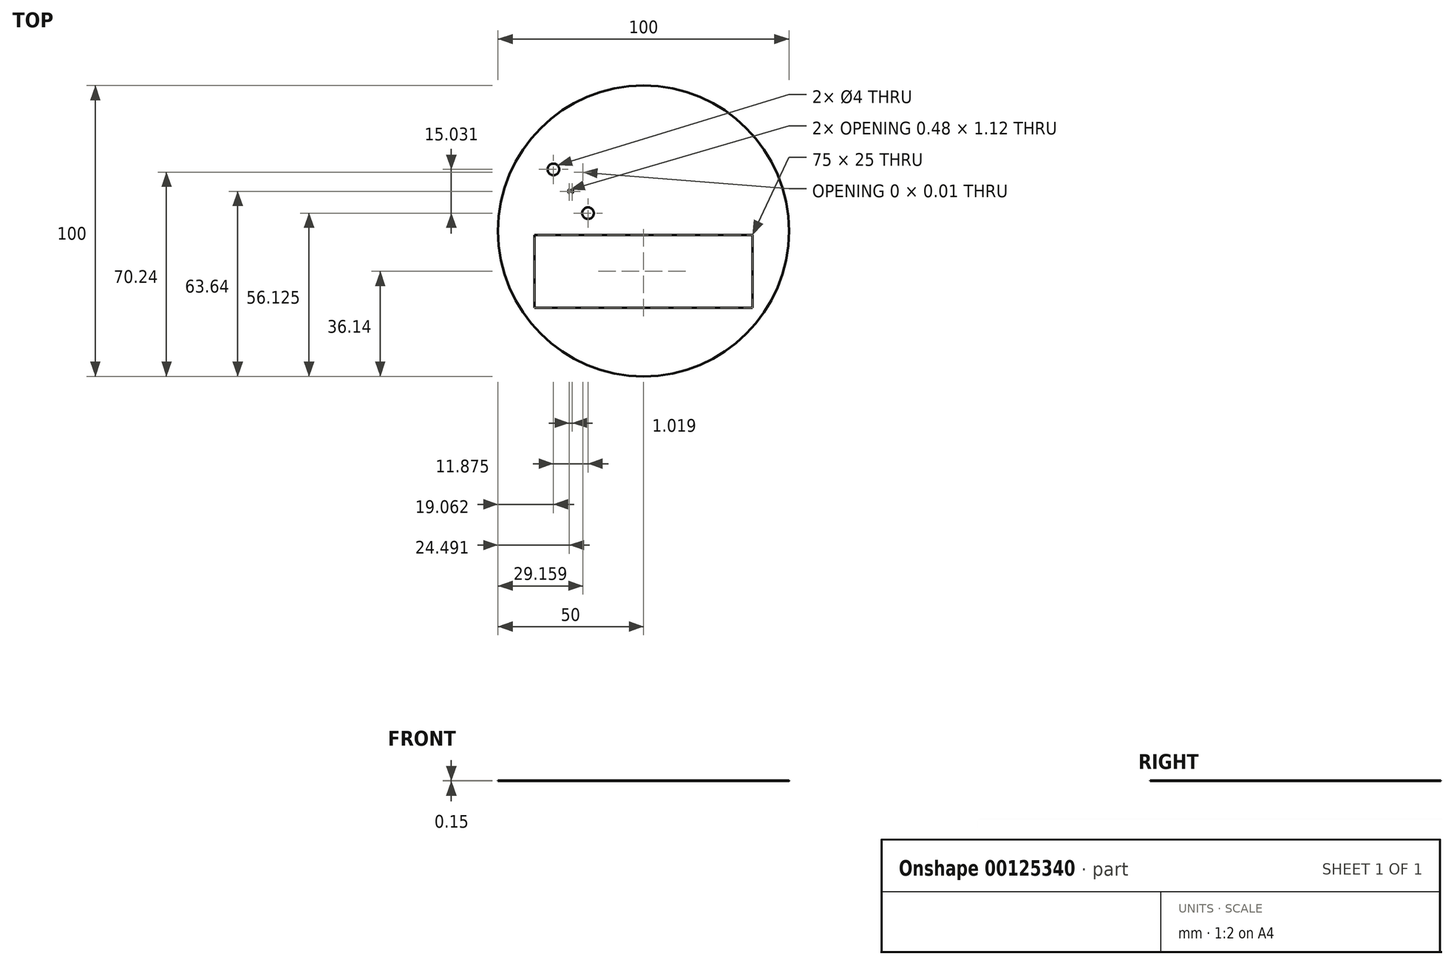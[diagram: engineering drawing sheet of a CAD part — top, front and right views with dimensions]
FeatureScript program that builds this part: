
annotation { "Feature Type Name" : "Feature", "Feature Type Description" : "" }
export const myFeature = defineFeature(function(context is Context, id is Id, definition is map)
    precondition{}
    {
        {
            var Q0;
            Q0=qCreatedBy(makeId("Top.planeOp"),FACE);
            var sketch = newSketch(context, id + "F0", { "sketchPlane" : qUnion([Q0])});
            skLineSegment(sketch, "E0.bottom", {"start": v(-37.5, 40) * mm, "end": v(37.5, 40) * mm});
            skLineSegment(sketch, "E0.top", {"start": v(-37.5, 15) * mm, "end": v(37.5, 15) * mm});
            skLineSegment(sketch, "E0.left", {"start": v(-37.5, 40) * mm, "end": v(-37.5, 15) * mm});
            skLineSegment(sketch, "E1.0", {"start": v(-37.5, 12.5) * mm, "end": v(37.5, 12.5) * mm});
            skLineSegment(sketch, "E2.top", {"start": v(-37.5, -12.5) * mm, "end": v(37.5, -12.5) * mm});
            skLineSegment(sketch, "E2.left", {"start": v(-37.5, 12.5) * mm, "end": v(-37.5, -12.5) * mm});
            skLineSegment(sketch, "E2.right", {"start": v(37.5, 12.5) * mm, "end": v(37.5, -12.5) * mm});
            skPoint(sketch, "E3.1.0.0", {"position": v(-17.06, 20.06) * mm});
            skPoint(sketch, "E3.1.0.4", {"position": v(-14.85, 26.8) * mm});
            skPoint(sketch, "E3.1.0.5", {"position": v(-25, 21.41) * mm});
            skLineSegment(sketch, "E3.1.0.10", {"start": v(-27.42, 30) * mm, "end": v(-29.86, 33.04) * mm});
            skPoint(sketch, "E3.1.0.11", {"position": v(-32.94, 20.06) * mm});
            skPoint(sketch, "E3.1.0.13", {"position": v(-25.75, 25) * mm});
            skPoint(sketch, "E3.1.0.15", {"position": v(-17.06, 34.94) * mm});
            skPoint(sketch, "E3.1.0.16", {"position": v(-24.49, 21.55) * mm});
            skLineSegment(sketch, "E3.1.0.17", {"start": v(-26.21, 24.92) * mm, "end": v(-29.12, 21.3) * mm});
            skLineSegment(sketch, "E3.1.0.19", {"start": v(-26.21, 30.08) * mm, "end": v(-29.1, 33.69) * mm});
            skLineSegment(sketch, "E3.1.0.20", {"start": v(-27.42, 25) * mm, "end": v(-29.87, 21.96) * mm});
            skPoint(sketch, "E3.1.0.24", {"position": v(-20.15, 29.65) * mm});
            skPoint(sketch, "E3.1.0.25", {"position": v(-22.85, 25.35) * mm});
            skPoint(sketch, "E3.1.0.27", {"position": v(-35.15, 26.8) * mm});
            skPoint(sketch, "E3.1.0.31", {"position": v(-27.15, 29.65) * mm});
            skPoint(sketch, "E3.1.0.35", {"position": v(-25.75, 30) * mm});
            skPoint(sketch, "E3.1.0.36", {"position": v(-27.15, 25.35) * mm});
            skPoint(sketch, "E3.1.0.41", {"position": v(-32.94, 34.94) * mm});
            skLineSegment(sketch, "E3.1.0.42", {"start": v(-23.79, 30.08) * mm, "end": v(-20.88, 33.7) * mm});
            skArc(sketch, "E3.1.0.43", {"start": v(-29.91, 29.7) * mm, "mid": v(-30, 29.78) * mm, "end": v(-30.1, 29.86) * mm});
            skArc(sketch, "E3.1.0.44", {"start": v(-20.08, 25.27) * mm, "mid": v(-14.77, 27.37) * mm, "end": v(-19.9, 29.89) * mm});
            skCircle(sketch, "E3.1.0.45", {"center": v(-19.06, 19.98) * mm, "radius": 2 * mm});
            skLineSegment(sketch, "E3.1.0.46", {"start": v(-23.79, 24.92) * mm, "end": v(-20.88, 21.3) * mm});
            skCircle(sketch, "E3.1.0.47", {"center": v(-30.94, 19.98) * mm, "radius": 2 * mm});
            skPoint(sketch, "E3.1.0.50", {"position": v(-25, 33.59) * mm});
            skLineSegment(sketch, "E3.1.0.60", {"start": v(-22.58, 25) * mm, "end": v(-20.13, 21.96) * mm});
            skPoint(sketch, "E3.1.0.61", {"position": v(-27.15, 25.35) * mm});
            skPoint(sketch, "E3.1.0.62", {"position": v(-27.15, 29.65) * mm});
            skPoint(sketch, "E3.1.0.64", {"position": v(-22.85, 25.35) * mm});
            skLineSegment(sketch, "E3.1.0.68", {"start": v(-22.58, 30) * mm, "end": v(-20.14, 33.04) * mm});
            skPoint(sketch, "E3.1.0.69", {"position": v(-27.15, 25.35) * mm});
            skPoint(sketch, "E3.1.0.72", {"position": v(-27.15, 29.65) * mm});
            skLineSegment(sketch, "E3.1.0.78", {"start": v(-29.85, 29.65) * mm, "end": v(-29.86, 29.65) * mm});
            skPoint(sketch, "E3.1.0.79", {"position": v(-22.85, 29.65) * mm});
            skPoint(sketch, "E3.1.0.81", {"position": v(-22.85, 25.35) * mm});
            skPoint(sketch, "E3.1.0.85", {"position": v(-22.85, 25.35) * mm});
            skPoint(sketch, "E3.1.0.87", {"position": v(-27.15, 25.35) * mm});
            skPoint(sketch, "E3.1.0.88", {"position": v(-27.15, 29.65) * mm});
            skLineSegment(sketch, "E3.1.0.89", {"start": v(-22.15, 29.65) * mm, "end": v(-20.49, 29.65) * mm});
            skPoint(sketch, "E3.1.0.90", {"position": v(-25, 27.5) * mm});
            skPoint(sketch, "E3.1.0.92", {"position": v(-22.85, 29.65) * mm});
            skPoint(sketch, "E3.1.0.95", {"position": v(-22.85, 25.35) * mm});
            skPoint(sketch, "E3.1.0.98", {"position": v(-27.15, 29.65) * mm});
            skPoint(sketch, "E3.1.0.99", {"position": v(-27.15, 25.35) * mm});
            skPoint(sketch, "E3.1.0.100", {"position": v(-22.85, 29.65) * mm});
            skLineSegment(sketch, "E3.1.0.104", {"start": v(-25.75, 25.21) * mm, "end": v(-25.75, 29.79) * mm});
            skLineSegment(sketch, "E3.1.0.105", {"start": v(-24.25, 29.79) * mm, "end": v(-24.25, 28.19) * mm});
            skLineSegment(sketch, "E3.1.0.106", {"start": v(-24.6, 24.7) * mm, "end": v(-24.6, 23.58) * mm});
            skLineSegment(sketch, "E3.1.0.108", {"start": v(-22.41, 29.65) * mm, "end": v(-22.15, 29.65) * mm});
            skLineSegment(sketch, "E3.1.0.109", {"start": v(-24.04, 30) * mm, "end": v(-23.95, 30) * mm});
            skLineSegment(sketch, "E3.1.0.110", {"start": v(-25.4, 30.5) * mm, "end": v(-25.4, 30.3) * mm});
            skArc(sketch, "E3.1.0.111", {"start": v(-24.6, 30.3) * mm, "mid": v(-24.51, 30.09) * mm, "end": v(-24.3, 30) * mm});
            skArc(sketch, "E3.1.0.112", {"start": v(-25.4, 30.3) * mm, "mid": v(-25.49, 30.09) * mm, "end": v(-25.7, 30) * mm});
            skLineSegment(sketch, "E3.1.0.113", {"start": v(-24.6, 30.3) * mm, "end": v(-24.6, 31.42) * mm});
            skLineSegment(sketch, "E3.1.0.115", {"start": v(-24.25, 30) * mm, "end": v(-24.3, 30) * mm});
            skLineSegment(sketch, "E3.1.0.117", {"start": v(-25.96, 30) * mm, "end": v(-26.05, 30) * mm});
            skLineSegment(sketch, "E3.1.0.118", {"start": v(-25.4, 24.7) * mm, "end": v(-25.4, 24.5) * mm});
            skLineSegment(sketch, "E3.1.0.120", {"start": v(-25.96, 25) * mm, "end": v(-26.05, 25) * mm});
            skArc(sketch, "E3.1.0.123", {"start": v(-25.4, 24.7) * mm, "mid": v(-25.49, 24.91) * mm, "end": v(-25.7, 25) * mm});
            skLineSegment(sketch, "E3.1.0.125", {"start": v(-24.25, 25) * mm, "end": v(-24.3, 25) * mm});
            skLineSegment(sketch, "E3.1.0.128", {"start": v(-24.04, 25) * mm, "end": v(-23.95, 25) * mm});
            skArc(sketch, "E3.1.0.134", {"start": v(-24.6, 24.7) * mm, "mid": v(-24.51, 24.91) * mm, "end": v(-24.3, 25) * mm});
            skLineSegment(sketch, "E3.1.0.151", {"start": v(-27.59, 25.35) * mm, "end": v(-27.85, 25.35) * mm});
            skLineSegment(sketch, "E4", {"start": v(-25.4, 24.5) * mm, "end": v(-25.4, 23.58) * mm});
            skLineSegment(sketch, "E5.top", {"start": v(-22.41, 25.35) * mm, "end": v(-20.5, 25.35) * mm});
            skLineSegment(sketch, "E5.left", {"start": v(-22.85, 29.44) * mm, "end": v(-22.85, 25.56) * mm});
            skLineSegment(sketch, "E5.right", {"start": v(-20.15, 29.57) * mm, "end": v(-20.15, 25.42) * mm});
            skLineSegment(sketch, "E6.left", {"start": v(-29.85, 29.55) * mm, "end": v(-29.85, 25.42) * mm});
            skLineSegment(sketch, "E6.right", {"start": v(-27.15, 29.44) * mm, "end": v(-27.15, 25.56) * mm});
            skLineSegment(sketch, "E7", {"start": v(-25.75, 25) * mm, "end": v(-25.7, 25) * mm});
            skLineSegment(sketch, "E8", {"start": v(-25.75, 30) * mm, "end": v(-25.7, 30) * mm});
            skLineSegment(sketch, "E9", {"start": v(-29.85, 25.35) * mm, "end": v(-29.85, 25.34) * mm});
            skArc(sketch, "E10.filletArc", {"start": v(-22.41, 25.35) * mm, "mid": v(-22.6, 25.23) * mm, "end": v(-22.58, 25) * mm});
            skPoint(sketch, "E11.visualSharp", {"position": v(-23.85, 25) * mm});
            skArc(sketch, "E11.filletArc", {"start": v(-23.79, 24.92) * mm, "mid": v(-23.86, 24.98) * mm, "end": v(-23.95, 25) * mm});
            skArc(sketch, "E12.filletArc", {"start": v(-22.58, 30) * mm, "mid": v(-22.6, 29.77) * mm, "end": v(-22.41, 29.65) * mm});
            skPoint(sketch, "E13.visualSharp", {"position": v(-23.85, 30) * mm});
            skArc(sketch, "E13.filletArc", {"start": v(-23.95, 30) * mm, "mid": v(-23.86, 30.02) * mm, "end": v(-23.79, 30.08) * mm});
            skPoint(sketch, "E14.visualSharp", {"position": v(-26.15, 30) * mm});
            skArc(sketch, "E14.filletArc", {"start": v(-26.21, 30.08) * mm, "mid": v(-26.14, 30.02) * mm, "end": v(-26.05, 30) * mm});
            skPoint(sketch, "E15.visualSharp", {"position": v(-26.15, 25) * mm});
            skArc(sketch, "E15.filletArc", {"start": v(-26.05, 25) * mm, "mid": v(-26.14, 24.98) * mm, "end": v(-26.21, 24.92) * mm});
            skArc(sketch, "E16", {"start": v(-27.42, 25) * mm, "mid": v(-27.26, 25.27) * mm, "end": v(-27.15, 25.56) * mm});
            skArc(sketch, "E17", {"start": v(-27.15, 29.44) * mm, "mid": v(-27.22, 29.75) * mm, "end": v(-27.42, 30) * mm});
            skArc(sketch, "E18", {"start": v(-27.59, 29.65) * mm, "mid": v(-27.43, 29.78) * mm, "end": v(-27.42, 30) * mm});
            skArc(sketch, "E19", {"start": v(-27.42, 25) * mm, "mid": v(-27.4, 25.23) * mm, "end": v(-27.59, 25.35) * mm});
            skArc(sketch, "E20.MirrorCS", {"start": v(-22.58, 25) * mm, "mid": v(-22.6, 25.23) * mm, "end": v(-22.41, 25.35) * mm});
            skArc(sketch, "E21.MirrorCS", {"start": v(-22.85, 29.44) * mm, "mid": v(-22.78, 29.75) * mm, "end": v(-22.58, 30) * mm});
            skArc(sketch, "E22.MirrorCS", {"start": v(-22.58, 25) * mm, "mid": v(-22.74, 25.27) * mm, "end": v(-22.85, 25.56) * mm});
            skLineSegment(sketch, "E23", {"start": v(-22.41, 29.65) * mm, "end": v(-20.49, 29.65) * mm});
            skArc(sketch, "E24", {"start": v(-19.9, 25.1) * mm, "mid": v(-20.18, 25.26) * mm, "end": v(-20.5, 25.35) * mm});
            skArc(sketch, "E25", {"start": v(-20.13, 21.96) * mm, "mid": v(-19.95, 21.86) * mm, "end": v(-19.75, 21.86) * mm});
            skArc(sketch, "E26", {"start": v(-20.85, 20.88) * mm, "mid": v(-20.81, 21.1) * mm, "end": v(-20.88, 21.3) * mm});
            skLineSegment(sketch, "E27", {"start": v(-24.6, 23.58) * mm, "end": v(-24.6, 23.58) * mm});
            skArc(sketch, "E28.MirrorCS", {"start": v(-29.87, 21.96) * mm, "mid": v(-30.05, 21.86) * mm, "end": v(-30.25, 21.86) * mm});
            skArc(sketch, "E29.MirrorCS", {"start": v(-29.15, 20.88) * mm, "mid": v(-29.19, 21.1) * mm, "end": v(-29.12, 21.3) * mm});
            skArc(sketch, "E30.MirrorCS", {"start": v(-25.4, 23.58) * mm, "mid": v(-25.46, 23.37) * mm, "end": v(-25.61, 23.2) * mm});
            skArc(sketch, "E31", {"start": v(-24.6, 23.58) * mm, "mid": v(-24.54, 23.37) * mm, "end": v(-24.39, 23.2) * mm});
            skArc(sketch, "E32", {"start": v(-25.61, 23.2) * mm, "mid": v(-25, 21.41) * mm, "end": v(-24.39, 23.2) * mm});
            skLineSegment(sketch, "E33", {"start": v(-29.12, 21.3) * mm, "end": v(-29.12, 21.3) * mm});
            skLineSegment(sketch, "E34", {"start": v(-29.5, 25.34) * mm, "end": v(-27.85, 25.35) * mm});
            skArc(sketch, "E35.filletArc", {"start": v(-29.91, 25.27) * mm, "mid": v(-29.87, 25.34) * mm, "end": v(-29.85, 25.42) * mm});
            skArc(sketch, "E36.filletArc", {"start": v(-29.85, 29.55) * mm, "mid": v(-29.87, 29.63) * mm, "end": v(-29.91, 29.7) * mm});
            skLineSegment(sketch, "E37", {"start": v(-29.5, 29.65) * mm, "end": v(-27.59, 29.65) * mm});
            skArc(sketch, "E38", {"start": v(-30.1, 29.86) * mm, "mid": v(-35.1, 27.5) * mm, "end": v(-30.1, 25.1) * mm});
            skArc(sketch, "E39", {"start": v(-30.1, 29.86) * mm, "mid": v(-29.8, 29.72) * mm, "end": v(-29.5, 29.65) * mm});
            skArc(sketch, "E40", {"start": v(-30.27, 33.13) * mm, "mid": v(-32.26, 36.51) * mm, "end": v(-29.15, 34.12) * mm});
            skArc(sketch, "E41", {"start": v(-30.02, 33.24) * mm, "mid": v(-30.14, 33.18) * mm, "end": v(-30.27, 33.13) * mm});
            skArc(sketch, "E42", {"start": v(-29.15, 34.12) * mm, "mid": v(-29.52, 33.6) * mm, "end": v(-30.02, 33.24) * mm});
            skArc(sketch, "E43", {"start": v(-29.86, 33.04) * mm, "mid": v(-30.05, 33.13) * mm, "end": v(-30.27, 33.13) * mm});
            skArc(sketch, "E44", {"start": v(-29.15, 34.12) * mm, "mid": v(-29.19, 33.9) * mm, "end": v(-29.1, 33.69) * mm});
            skLineSegment(sketch, "E45", {"start": v(-25.4, 31.67) * mm, "end": v(-25.4, 31.67) * mm});
            skLineSegment(sketch, "E46", {"start": v(-25.4, 31.42) * mm, "end": v(-25.4, 30.5) * mm});
            skArc(sketch, "E47", {"start": v(-25.4, 31.42) * mm, "mid": v(-25.46, 31.64) * mm, "end": v(-25.62, 31.8) * mm});
            skArc(sketch, "E48", {"start": v(-24.38, 31.8) * mm, "mid": v(-25, 33.59) * mm, "end": v(-25.62, 31.8) * mm});
            skArc(sketch, "E49", {"start": v(-24.38, 31.8) * mm, "mid": v(-24.53, 31.64) * mm, "end": v(-24.6, 31.42) * mm});
            skArc(sketch, "E50.filletArc", {"start": v(-25.75, 29.79) * mm, "mid": v(-25.81, 29.94) * mm, "end": v(-25.96, 30) * mm});
            skLineSegment(sketch, "E51", {"start": v(-25.96, 30) * mm, "end": v(-25.75, 30) * mm});
            skPoint(sketch, "E52.visualSharp", {"position": v(-24.25, 30) * mm});
            skArc(sketch, "E52.filletArc", {"start": v(-24.04, 30) * mm, "mid": v(-24.19, 29.94) * mm, "end": v(-24.25, 29.79) * mm});
            skLineSegment(sketch, "E53", {"start": v(-24.25, 30) * mm, "end": v(-24.04, 30) * mm});
            skArc(sketch, "E54", {"start": v(-20.84, 34.1) * mm, "mid": v(-20.79, 34) * mm, "end": v(-20.72, 33.9) * mm});
            skArc(sketch, "E55", {"start": v(-20.72, 33.9) * mm, "mid": v(-20.4, 33.52) * mm, "end": v(-19.98, 33.24) * mm});
            skArc(sketch, "E56", {"start": v(-20.88, 33.7) * mm, "mid": v(-20.8, 33.9) * mm, "end": v(-20.84, 34.1) * mm});
            skArc(sketch, "E57", {"start": v(-19.73, 33.13) * mm, "mid": v(-17.75, 36.52) * mm, "end": v(-20.84, 34.1) * mm});
            skArc(sketch, "E58", {"start": v(-19.98, 33.24) * mm, "mid": v(-19.86, 33.18) * mm, "end": v(-19.73, 33.13) * mm});
            skArc(sketch, "E59", {"start": v(-19.73, 33.13) * mm, "mid": v(-19.94, 33.13) * mm, "end": v(-20.14, 33.04) * mm});
            skArc(sketch, "E60", {"start": v(-19.9, 29.89) * mm, "mid": v(-20, 29.8) * mm, "end": v(-20.08, 29.72) * mm});
            skLineSegment(sketch, "E61", {"start": v(-20.15, 29.65) * mm, "end": v(-20.15, 29.65) * mm});
            skArc(sketch, "E62", {"start": v(-20.49, 29.65) * mm, "mid": v(-20.18, 29.74) * mm, "end": v(-19.9, 29.89) * mm});
            skArc(sketch, "E63.filletArc", {"start": v(-20.08, 29.72) * mm, "mid": v(-20.13, 29.65) * mm, "end": v(-20.15, 29.57) * mm});
            skArc(sketch, "E64.filletArc", {"start": v(-20.15, 25.42) * mm, "mid": v(-20.13, 25.34) * mm, "end": v(-20.08, 25.27) * mm});
            skPoint(sketch, "E65.visualSharp", {"position": v(-24.25, 25) * mm});
            skArc(sketch, "E65.filletArc", {"start": v(-24.25, 25.21) * mm, "mid": v(-24.19, 25.06) * mm, "end": v(-24.04, 25) * mm});
            skLineSegment(sketch, "E66", {"start": v(-24.25, 25) * mm, "end": v(-24.04, 25) * mm});
            skLineSegment(sketch, "E67", {"start": v(-24.25, 25.21) * mm, "end": v(-24.25, 26.81) * mm});
            skArc(sketch, "E68.filletArc", {"start": v(-25.96, 25) * mm, "mid": v(-25.81, 25.06) * mm, "end": v(-25.75, 25.21) * mm});
            skLineSegment(sketch, "E69", {"start": v(-25.96, 25) * mm, "end": v(-25.75, 25) * mm});
            skArc(sketch, "E70", {"start": v(-30.1, 25.1) * mm, "mid": v(-30, 25.19) * mm, "end": v(-29.91, 25.27) * mm});
            skLineSegment(sketch, "E71", {"start": v(-29.91, 25.27) * mm, "end": v(-29.91, 25.27) * mm});
            skArc(sketch, "E72", {"start": v(-29.5, 25.34) * mm, "mid": v(-29.82, 25.26) * mm, "end": v(-30.1, 25.1) * mm});
            skLineSegment(sketch, "E73", {"start": v(-25, 32.59) * mm, "end": v(-25, 22.41) * mm});
            skPoint(sketch, "E74.endSnap0", {"position": v(-24.25, 27.5) * mm});
            skLineSegment(sketch, "E75", {"start": v(-24.72, 27.46) * mm, "end": v(-24.34, 26.96) * mm});
            skPoint(sketch, "E76.newPointB", {"position": v(-24.25, 25.21) * mm});
            skPoint(sketch, "E77.visualSharp", {"position": v(-24.75, 27.5) * mm});
            skArc(sketch, "E77.filletArc", {"start": v(-24.72, 27.54) * mm, "mid": v(-24.73, 27.52) * mm, "end": v(-24.73, 27.5) * mm});
            skArc(sketch, "E78.filletArc", {"start": v(-24.34, 26.96) * mm, "mid": v(-24.28, 26.94) * mm, "end": v(-24.25, 26.99) * mm});
            skLineSegment(sketch, "E79", {"start": v(-24.25, 27.5) * mm, "end": v(-24.25, 26.99) * mm});
            skArc(sketch, "E80", {"start": v(-24.73, 27.5) * mm, "mid": v(-24.73, 27.48) * mm, "end": v(-24.72, 27.46) * mm});
            skLineSegment(sketch, "E81.MirrorCS", {"start": v(-24.72, 27.54) * mm, "end": v(-24.34, 28.04) * mm});
            skArc(sketch, "E82.MirrorCS", {"start": v(-24.34, 28.04) * mm, "mid": v(-24.28, 28.06) * mm, "end": v(-24.25, 28.01) * mm});
            skLineSegment(sketch, "E83.MirrorCS", {"start": v(-24.25, 27.5) * mm, "end": v(-24.25, 28.01) * mm});
            skLineSegment(sketch, "E84", {"start": v(-24.25, 26.81) * mm, "end": v(-24.25, 26.99) * mm});
            skLineSegment(sketch, "E85", {"start": v(-24.25, 28.19) * mm, "end": v(-24.25, 28.01) * mm});
            skLineSegment(sketch, "E86.MirrorCS", {"start": v(-25.28, 27.54) * mm, "end": v(-25.66, 28.04) * mm});
            skArc(sketch, "E87.MirrorCS", {"start": v(-25.66, 28.04) * mm, "mid": v(-25.72, 28.06) * mm, "end": v(-25.75, 28.01) * mm});
            skArc(sketch, "E88.MirrorCS", {"start": v(-25.28, 27.54) * mm, "mid": v(-25.27, 27.52) * mm, "end": v(-25.27, 27.5) * mm});
            skArc(sketch, "E89.MirrorCS", {"start": v(-25.27, 27.5) * mm, "mid": v(-25.27, 27.48) * mm, "end": v(-25.28, 27.46) * mm});
            skLineSegment(sketch, "E90.MirrorCS", {"start": v(-25.28, 27.46) * mm, "end": v(-25.66, 26.96) * mm});
            skArc(sketch, "E91.MirrorCS", {"start": v(-25.66, 26.96) * mm, "mid": v(-25.72, 26.94) * mm, "end": v(-25.75, 26.99) * mm});
            skCircle(sketch, "E92", {"center": v(0, 13.86) * mm, "radius": 50 * mm});
            skLineSegment(sketch, "E93", {"start": v(37.5, 40) * mm, "end": v(37.5, 15) * mm});
            skSolve(sketch);
        }
        {
            var Q0;
            Q0=makeQuery(id+"F0.imprint","IMPRINT",FACE,{"disambiguationData":[TD([[makeQuery(id+"F0.imprint","IMPRINT",EDGE,{"derivedFrom":sQuery(id+"F0.wireOp",EDGE,"E0.bottom")}),1.0]])]});
            var Q1;
            {var subQ4=sQuery(id+"F0.wireOp",EDGE,"E55");Q1=makeQuery(id+"F0.imprint","IMPRINT",FACE,{"disambiguationData":[TD([[makeQuery(id+"F0.imprint","IMPRINT",EDGE,{"derivedFrom":subQ4}),1.0]])]});}
            var Q2;
            Q2=makeQuery(id+"F0.imprint","IMPRINT",FACE,{"disambiguationData":[TD([[makeQuery(id+"F0.imprint","IMPRINT",EDGE,{"derivedFrom":sQuery(id+"F0.wireOp",EDGE,"E5.right")}),1.0]])]});
            var Q3;
            {var subQ0=sQuery(id+"F0.wireOp",EDGE,"E3.1.0.45");var subQ1=makeQuery(id+"F0.imprint","INTERSECT",VERTEX,{"derivedFrom":[subQ0,sQuery(id+"F0.wireOp",EDGE,"E25")]});Q3=makeQuery(id+"F0.imprint","IMPRINT",FACE,{"disambiguationData":[TD([[makeQuery(id+"F0.imprint","IMPRINT",EDGE,{"disambiguationData":[TD([[subQ1,1.0]])],"derivedFrom":subQ0}),-1.0]])]});}
            var Q4;
            Q4=makeQuery(id+"F0.imprint","IMPRINT",FACE,{"disambiguationData":[TD([[makeQuery(id+"F0.imprint","IMPRINT",EDGE,{"derivedFrom":sQuery(id+"F0.wireOp",EDGE,"E3.1.0.43")}),1.0]])]});
            var Q5;
            Q5=makeQuery(id+"F0.imprint","IMPRINT",FACE,{"disambiguationData":[TD([[makeQuery(id+"F0.imprint","IMPRINT",EDGE,{"derivedFrom":sQuery(id+"F0.wireOp",EDGE,"E40")}),-1.0]])]});
            var Q6;
            Q6=makeQuery(id+"F0.imprint","IMPRINT",FACE,{"disambiguationData":[TD([[makeQuery(id+"F0.imprint","IMPRINT",EDGE,{"derivedFrom":sQuery(id+"F0.wireOp",EDGE,"E3.1.0.43")}),-1.0]])]});
            var Q7;
            Q7=makeQuery(id+"F0.imprint","IMPRINT",FACE,{"disambiguationData":[TD([[makeQuery(id+"F0.imprint","IMPRINT",EDGE,{"derivedFrom":sQuery(id+"F0.wireOp",EDGE,"E3.1.0.10")}),-1.0]])]});
            var Q8;
            Q8=makeQuery(id+"F0.imprint","IMPRINT",FACE,{"disambiguationData":[TD([[makeQuery(id+"F0.imprint","IMPRINT",EDGE,{"derivedFrom":sQuery(id+"F0.wireOp",EDGE,"E3.1.0.105")}),-1.0]])]});
            var Q9;
            {var subQ1=sQuery(id+"F0.wireOp",EDGE,"E3.1.0.42");Q9=makeQuery(id+"F0.imprint","IMPRINT",FACE,{"disambiguationData":[TD([[makeQuery(id+"F0.imprint","IMPRINT",EDGE,{"derivedFrom":subQ1}),-1.0]])]});}
            var Q10;
            Q10=makeQuery(id+"F0.imprint","IMPRINT",FACE,{"disambiguationData":[TD([[makeQuery(id+"F0.imprint","IMPRINT",EDGE,{"derivedFrom":sQuery(id+"F0.wireOp",EDGE,"E5.top")}),1.0]])]});
            var Q11;
            {var subQ0=sQuery(id+"F0.wireOp",EDGE,"E3.1.0.47");var subQ1=makeQuery(id+"F0.imprint","INTERSECT",VERTEX,{"derivedFrom":[subQ0,sQuery(id+"F0.wireOp",EDGE,"E28.MirrorCS")]});Q11=makeQuery(id+"F0.imprint","IMPRINT",FACE,{"disambiguationData":[TD([[makeQuery(id+"F0.imprint","IMPRINT",EDGE,{"disambiguationData":[TD([[subQ1,1.0]])],"derivedFrom":subQ0}),1.0]])]});}
            extrude(context, id + "F1", {"entities" : qUnion([Q0, Q1, Q2, Q3, Q4, Q5, Q6, Q7, Q8, Q9, Q10, Q11]), "depth" : .15 * mm});
        }
    });
